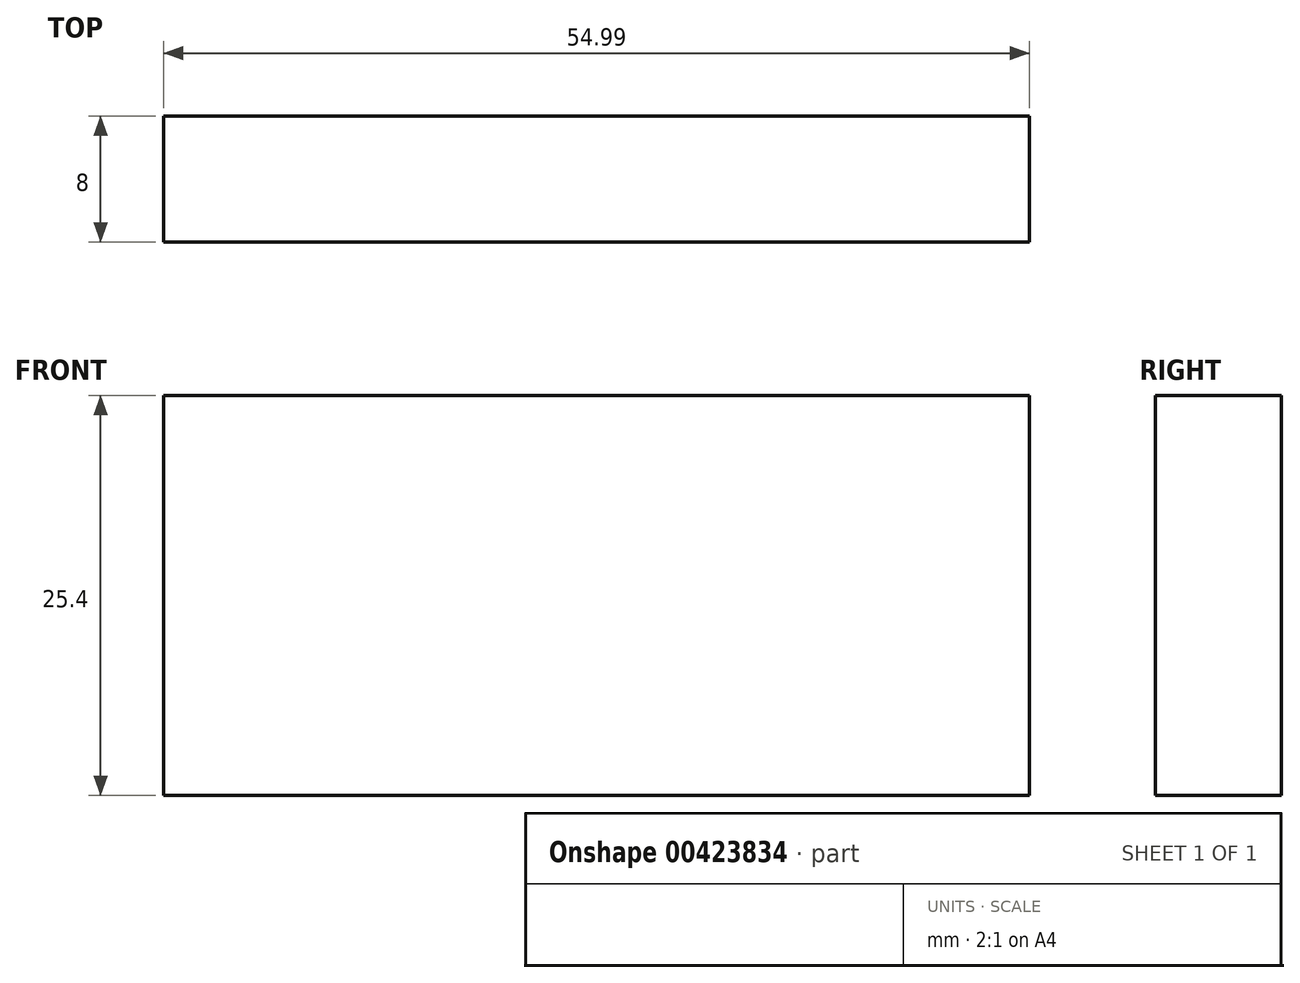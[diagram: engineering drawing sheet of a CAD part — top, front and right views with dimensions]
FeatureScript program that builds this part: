
annotation { "Feature Type Name" : "Feature", "Feature Type Description" : "" }
export const myFeature = defineFeature(function(context is Context, id is Id, definition is map)
    precondition{}
    {
        {
            var Q0;
            Q0=qCreatedBy(makeId("Front.planeOp"),FACE);
            var sketch = newSketch(context, id + "F0", { "sketchPlane" : qUnion([Q0])});
            skLineSegment(sketch, "E0", {"start": v(-37.16, -14.7) * mm, "end": v(17.83, -14.7) * mm});
            skLineSegment(sketch, "E1", {"start": v(17.83, -14.7) * mm, "end": v(17.83, 10.7) * mm});
            skLineSegment(sketch, "E2", {"start": v(-37.16, -14.7) * mm, "end": v(-37.16, 10.7) * mm});
            skLineSegment(sketch, "E3", {"start": v(-37.16, 10.7) * mm, "end": v(17.83, 10.7) * mm});
            skSolve(sketch);
        }
        {
            var Q0;
            Q0=makeQuery(id+"F0.imprint","IMPRINT",FACE,{"disambiguationData":[TD([[makeQuery(id+"F0.imprint","IMPRINT",EDGE,{"derivedFrom":sQuery(id+"F0.wireOp",EDGE,"E0")}),1.0]])]});
            extrude(context, id + "F1", {"entities" : qUnion([Q0]), "depth" : 8 * mm});
        }
    });
